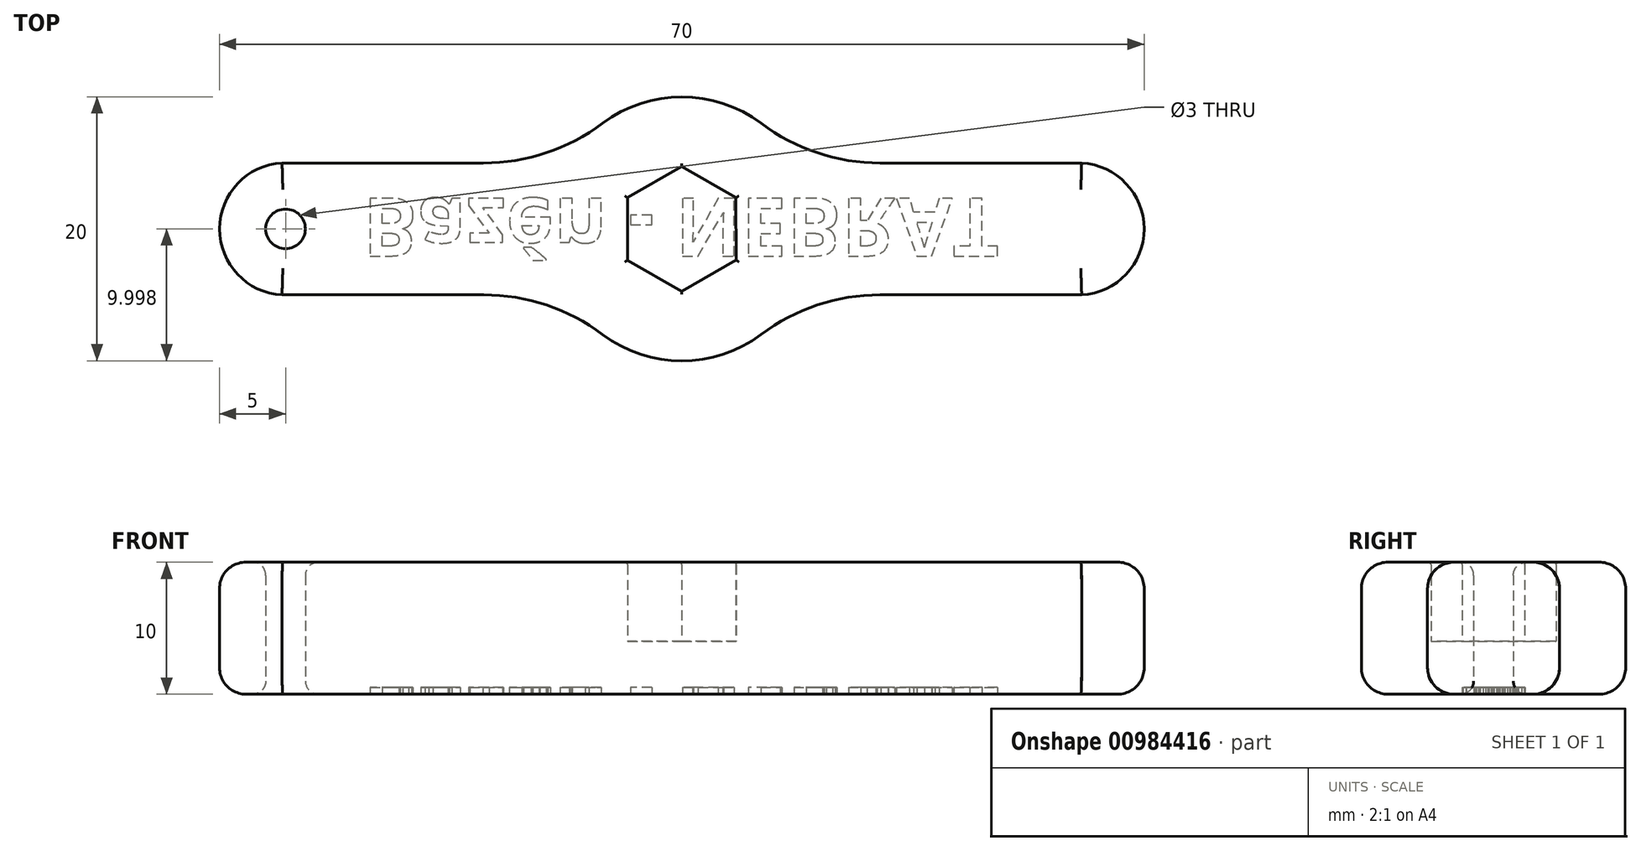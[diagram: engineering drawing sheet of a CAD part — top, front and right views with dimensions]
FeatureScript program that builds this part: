
annotation { "Feature Type Name" : "Feature", "Feature Type Description" : "" }
export const myFeature = defineFeature(function(context is Context, id is Id, definition is map)
    precondition{}
    {
        {
            var Q0;
            Q0=qCreatedBy(makeId("Top.planeOp"),FACE);
            var sketch = newSketch(context, id + "F0", { "sketchPlane" : qUnion([Q0])});
            skCircle(sketch, "E0.cCircle", {"center": v(0, 0) * mm, "radius": 4.1 * mm, "construction": true});
            skLineSegment(sketch, "E0.0", {"start": v(4.1, -2.36) * mm, "end": v(0, -4.73) * mm});
            skLineSegment(sketch, "E0.1", {"start": v(0, -4.73) * mm, "end": v(-4.1, -2.37) * mm});
            skLineSegment(sketch, "E0.2", {"start": v(-4.1, -2.37) * mm, "end": v(-4.1, 2.36) * mm});
            skLineSegment(sketch, "E0.3", {"start": v(-4.1, 2.36) * mm, "end": v(0, 4.73) * mm});
            skLineSegment(sketch, "E0.4", {"start": v(0, 4.73) * mm, "end": v(4.1, 2.37) * mm});
            skLineSegment(sketch, "E0.5", {"start": v(4.1, 2.37) * mm, "end": v(4.1, -2.36) * mm});
            skPoint(sketch, "E0.0.midPoint", {"position": v(2.05, -3.55) * mm});
            skArc(sketch, "E1", {"start": v(6, 8) * mm, "mid": v(0, 10) * mm, "end": v(-6, 8) * mm});
            skArc(sketch, "E2", {"start": v(29.73, -5) * mm, "mid": v(35, 0) * mm, "end": v(29.73, 5) * mm});
            skPoint(sketch, "E2.centerSnap0", {"position": v(-4.1, 0) * mm});
            skLineSegment(sketch, "E3", {"start": v(30.27, 5) * mm, "end": v(15.01, 5) * mm});
            skLineSegment(sketch, "E4", {"start": v(30.27, -5) * mm, "end": v(15, -5) * mm});
            skPoint(sketch, "E5.visualSharp", {"position": v(8.67, 5) * mm});
            skArc(sketch, "E5.filletArc", {"start": v(6, 8) * mm, "mid": v(10.26, 5.76) * mm, "end": v(15.01, 5) * mm});
            skPoint(sketch, "E6.visualSharp", {"position": v(8.66, -5) * mm});
            skArc(sketch, "E6.filletArc", {"start": v(15, -5) * mm, "mid": v(10.26, -5.77) * mm, "end": v(6, -8) * mm});
            skArc(sketch, "E7.MirrorCS", {"start": v(-6, 8) * mm, "mid": v(-10.26, 5.76) * mm, "end": v(-15.01, 5) * mm});
            skLineSegment(sketch, "E8.MirrorCS", {"start": v(-30.27, 5) * mm, "end": v(-15.01, 5) * mm});
            skArc(sketch, "E9.MirrorCS", {"start": v(-29.73, -5) * mm, "mid": v(-35, 0) * mm, "end": v(-29.73, 5) * mm});
            skLineSegment(sketch, "E10.MirrorCS", {"start": v(-30.27, -5) * mm, "end": v(-15, -5) * mm});
            skArc(sketch, "E11.MirrorCS", {"start": v(-15, -5) * mm, "mid": v(-10.26, -5.77) * mm, "end": v(-6, -8) * mm});
            skArc(sketch, "E12.trimOffspring", {"start": v(-6, -8) * mm, "mid": v(0, -10) * mm, "end": v(6, -8) * mm});
            skCircle(sketch, "E13", {"center": v(-30, 0) * mm, "radius": 1.5 * mm});
            skSolve(sketch);
        }
        {
            var Q0;
            Q0=makeQuery(id+"F0.imprint","IMPRINT",FACE,{"disambiguationData":[TD([[makeQuery(id+"F0.imprint","IMPRINT",EDGE,{"derivedFrom":sQuery(id+"F0.wireOp",EDGE,"E0.0")}),1.0]])]});
            extrude(context, id + "F1", {"entities" : qUnion([Q0]), "depth" : 10 * mm, "offsetDistance" : 25 * mm, "symmetric" : true});
        }
        {
            var Q0;
            Q0=makeQuery(id+"F1.opExtrude","CAP_FACE",FACE,{"disambiguationData":[OSD([sQuery(id+"F0.wireOp",EDGE,"E0.0"),sQuery(id+"F0.wireOp",EDGE,"E0.1"),sQuery(id+"F0.wireOp",EDGE,"E0.2"),sQuery(id+"F0.wireOp",EDGE,"E0.3"),sQuery(id+"F0.wireOp",EDGE,"E0.4"),sQuery(id+"F0.wireOp",EDGE,"E0.5"),sQuery(id+"F0.wireOp",EDGE,"E1"),sQuery(id+"F0.wireOp",EDGE,"E2"),sQuery(id+"F0.wireOp",EDGE,"E3"),sQuery(id+"F0.wireOp",EDGE,"E4"),sQuery(id+"F0.wireOp",EDGE,"E5.filletArc"),sQuery(id+"F0.wireOp",EDGE,"E6.filletArc"),sQuery(id+"F0.wireOp",EDGE,"E7.MirrorCS"),sQuery(id+"F0.wireOp",EDGE,"E8.MirrorCS"),sQuery(id+"F0.wireOp",EDGE,"E9.MirrorCS"),sQuery(id+"F0.wireOp",EDGE,"E10.MirrorCS"),sQuery(id+"F0.wireOp",EDGE,"E11.MirrorCS"),sQuery(id+"F0.wireOp",EDGE,"E12.trimOffspring")])],"isStart":true});
            var sketch = newSketch(context, id + "F2", { "sketchPlane" : qUnion([Q0])});
            skCircle(sketch, "E14", {"center": v(0, 0) * mm, "radius": 7.22 * mm});
            skSolve(sketch);
        }
        {
            var Q0;
            Q0 = qSketchRegion(id + "F2", true);
            extrude(context, id + "F3", {"entities" : qUnion([Q0]), "operationType" : NewBodyOperationType.ADD, "oppositeDirection" : true, "depth" : 4 * mm, "offsetDistance" : 25 * mm});
        }
        {
            var Q0;
            Q0=makeQuery(id+"F1.opExtrude","CAP_EDGE",EDGE,{"disambiguationData":[OSD([sQuery(id+"F0.wireOp",EDGE,"E0.3")])],"isStart":false});
            var Q1;
            Q1=makeQuery(id+"F1.opExtrude","CAP_EDGE",EDGE,{"disambiguationData":[OSD([sQuery(id+"F0.wireOp",EDGE,"E0.4")])],"isStart":false});
            var Q2;
            Q2=makeQuery(id+"F1.opExtrude","CAP_EDGE",EDGE,{"disambiguationData":[OSD([sQuery(id+"F0.wireOp",EDGE,"E0.5")])],"isStart":false});
            var Q3;
            Q3=makeQuery(id+"F1.opExtrude","CAP_EDGE",EDGE,{"disambiguationData":[OSD([sQuery(id+"F0.wireOp",EDGE,"E0.0")])],"isStart":false});
            var Q4;
            Q4=makeQuery(id+"F1.opExtrude","CAP_EDGE",EDGE,{"disambiguationData":[OSD([sQuery(id+"F0.wireOp",EDGE,"E0.1")])],"isStart":false});
            var Q5;
            Q5=makeQuery(id+"F1.opExtrude","CAP_EDGE",EDGE,{"disambiguationData":[OSD([sQuery(id+"F0.wireOp",EDGE,"E0.2")])],"isStart":false});
            fillet(context, id + "F4", {"entities" : qUnion([Q0, Q1, Q2, Q3, Q4, Q5]), "radius" : 0.2 * mm, "tangentPropagation" : true, "allowEdgeOverflow" : false});
        }
        {
            var Q0;
            Q0=makeQuery(id+"F3.boolean.opBoolean","MERGE",FACE,{"derivedFrom":[makeQuery(id+"F1.opExtrude","CAP_FACE",FACE,{"disambiguationData":[OSD([sQuery(id+"F0.wireOp",EDGE,"E0.0"),sQuery(id+"F0.wireOp",EDGE,"E0.1"),sQuery(id+"F0.wireOp",EDGE,"E0.2"),sQuery(id+"F0.wireOp",EDGE,"E0.3"),sQuery(id+"F0.wireOp",EDGE,"E0.4"),sQuery(id+"F0.wireOp",EDGE,"E0.5"),sQuery(id+"F0.wireOp",EDGE,"E1"),sQuery(id+"F0.wireOp",EDGE,"E2"),sQuery(id+"F0.wireOp",EDGE,"E3"),sQuery(id+"F0.wireOp",EDGE,"E4"),sQuery(id+"F0.wireOp",EDGE,"E5.filletArc"),sQuery(id+"F0.wireOp",EDGE,"E6.filletArc"),sQuery(id+"F0.wireOp",EDGE,"E7.MirrorCS"),sQuery(id+"F0.wireOp",EDGE,"E8.MirrorCS"),sQuery(id+"F0.wireOp",EDGE,"E9.MirrorCS"),sQuery(id+"F0.wireOp",EDGE,"E10.MirrorCS"),sQuery(id+"F0.wireOp",EDGE,"E11.MirrorCS"),sQuery(id+"F0.wireOp",EDGE,"E12.trimOffspring")])],"isStart":true}),makeQuery(id+"F3.opExtrude","CAP_FACE",FACE,{"disambiguationData":[OSD([sQuery(id+"F2.wireOp",EDGE,"E14")])],"isStart":true})]});
            var sketch = newSketch(context, id + "F5", { "sketchPlane" : qUnion([Q0])});
            skText(sketch, "E15", { "text": "Bazén - NEBRAT", "fontName": "OpenSans-Bold.ttf"});
            const initialGuessF5  = {"E15": [-0.02415, -0.00232, 1, 0, 0.00442]};
            skSetInitialGuess(sketch, initialGuessF5);
            skSolve(sketch);
        }
        {
            var Q0;
            Q0 = qSketchRegion(id + "F5", true);
            extrude(context, id + "F6", {"entities" : qUnion([Q0]), "operationType" : NewBodyOperationType.REMOVE, "oppositeDirection" : true, "depth" : 0.5 * mm, "offsetDistance" : 25 * mm});
        }
        {
            var Q0;
            Q0=makeQuery(id+"F1.opExtrude","CAP_EDGE",EDGE,{"disambiguationData":[OSD([sQuery(id+"F0.wireOp",EDGE,"E13")])],"isStart":false});
            fillet(context, id + "F7", {"entities" : qUnion([Q0]), "radius" : 1 * mm, "tangentPropagation" : true, "allowEdgeOverflow" : false});
        }
        {
            var Q0;
            Q0=makeQuery(id+"F1.opExtrude","CAP_EDGE",EDGE,{"disambiguationData":[OSD([sQuery(id+"F0.wireOp",EDGE,"E2")])],"isStart":true});
            var Q1;
            Q1=makeQuery(id+"F1.opExtrude","CAP_EDGE",EDGE,{"disambiguationData":[OSD([sQuery(id+"F0.wireOp",EDGE,"E3")])],"isStart":true});
            var Q2;
            Q2=makeQuery(id+"F1.opExtrude","CAP_EDGE",EDGE,{"disambiguationData":[OSD([sQuery(id+"F0.wireOp",EDGE,"E5.filletArc")])],"isStart":true});
            var Q3;
            Q3=makeQuery(id+"F1.opExtrude","CAP_EDGE",EDGE,{"disambiguationData":[OSD([sQuery(id+"F0.wireOp",EDGE,"E1")])],"isStart":true});
            var Q4;
            Q4=makeQuery(id+"F1.opExtrude","CAP_EDGE",EDGE,{"disambiguationData":[OSD([sQuery(id+"F0.wireOp",EDGE,"E7.MirrorCS")])],"isStart":true});
            var Q5;
            Q5=makeQuery(id+"F1.opExtrude","CAP_EDGE",EDGE,{"disambiguationData":[OSD([sQuery(id+"F0.wireOp",EDGE,"E8.MirrorCS")])],"isStart":true});
            var Q6;
            Q6=makeQuery(id+"F1.opExtrude","CAP_EDGE",EDGE,{"disambiguationData":[OSD([sQuery(id+"F0.wireOp",EDGE,"E9.MirrorCS")])],"isStart":true});
            var Q7;
            Q7=makeQuery(id+"F1.opExtrude","CAP_EDGE",EDGE,{"disambiguationData":[OSD([sQuery(id+"F0.wireOp",EDGE,"E10.MirrorCS")])],"isStart":true});
            var Q8;
            Q8=makeQuery(id+"F1.opExtrude","CAP_EDGE",EDGE,{"disambiguationData":[OSD([sQuery(id+"F0.wireOp",EDGE,"E11.MirrorCS")])],"isStart":true});
            var Q9;
            Q9=makeQuery(id+"F1.opExtrude","CAP_EDGE",EDGE,{"disambiguationData":[OSD([sQuery(id+"F0.wireOp",EDGE,"E12.trimOffspring")])],"isStart":true});
            var Q10;
            Q10=makeQuery(id+"F1.opExtrude","CAP_EDGE",EDGE,{"disambiguationData":[OSD([sQuery(id+"F0.wireOp",EDGE,"E6.filletArc")])],"isStart":true});
            var Q11;
            Q11=makeQuery(id+"F1.opExtrude","CAP_EDGE",EDGE,{"disambiguationData":[OSD([sQuery(id+"F0.wireOp",EDGE,"E4")])],"isStart":true});
            var Q12;
            Q12=makeQuery(id+"F1.opExtrude","CAP_EDGE",EDGE,{"disambiguationData":[OSD([sQuery(id+"F0.wireOp",EDGE,"E8.MirrorCS")])],"isStart":false});
            var Q13;
            Q13=makeQuery(id+"F1.opExtrude","CAP_EDGE",EDGE,{"disambiguationData":[OSD([sQuery(id+"F0.wireOp",EDGE,"E7.MirrorCS")])],"isStart":false});
            var Q14;
            Q14=makeQuery(id+"F1.opExtrude","CAP_EDGE",EDGE,{"disambiguationData":[OSD([sQuery(id+"F0.wireOp",EDGE,"E1")])],"isStart":false});
            var Q15;
            Q15=makeQuery(id+"F1.opExtrude","CAP_EDGE",EDGE,{"disambiguationData":[OSD([sQuery(id+"F0.wireOp",EDGE,"E5.filletArc")])],"isStart":false});
            var Q16;
            Q16=makeQuery(id+"F1.opExtrude","CAP_EDGE",EDGE,{"disambiguationData":[OSD([sQuery(id+"F0.wireOp",EDGE,"E3")])],"isStart":false});
            var Q17;
            Q17=makeQuery(id+"F1.opExtrude","CAP_EDGE",EDGE,{"disambiguationData":[OSD([sQuery(id+"F0.wireOp",EDGE,"E2")])],"isStart":false});
            var Q18;
            Q18=makeQuery(id+"F1.opExtrude","CAP_EDGE",EDGE,{"disambiguationData":[OSD([sQuery(id+"F0.wireOp",EDGE,"E4")])],"isStart":false});
            var Q19;
            Q19=makeQuery(id+"F1.opExtrude","CAP_EDGE",EDGE,{"disambiguationData":[OSD([sQuery(id+"F0.wireOp",EDGE,"E6.filletArc")])],"isStart":false});
            var Q20;
            Q20=makeQuery(id+"F1.opExtrude","CAP_EDGE",EDGE,{"disambiguationData":[OSD([sQuery(id+"F0.wireOp",EDGE,"E12.trimOffspring")])],"isStart":false});
            var Q21;
            Q21=makeQuery(id+"F1.opExtrude","CAP_EDGE",EDGE,{"disambiguationData":[OSD([sQuery(id+"F0.wireOp",EDGE,"E11.MirrorCS")])],"isStart":false});
            var Q22;
            Q22=makeQuery(id+"F1.opExtrude","CAP_EDGE",EDGE,{"disambiguationData":[OSD([sQuery(id+"F0.wireOp",EDGE,"E10.MirrorCS")])],"isStart":false});
            var Q23;
            Q23=makeQuery(id+"F1.opExtrude","CAP_EDGE",EDGE,{"disambiguationData":[OSD([sQuery(id+"F0.wireOp",EDGE,"E9.MirrorCS")])],"isStart":false});
            fillet(context, id + "F8", {"entities" : qUnion([Q0, Q1, Q2, Q3, Q4, Q5, Q6, Q7, Q8, Q9, Q10, Q11, Q12, Q13, Q14, Q15, Q16, Q17, Q18, Q19, Q20, Q21, Q22, Q23]), "radius" : 2 * mm, "tangentPropagation" : true, "allowEdgeOverflow" : false});
        }
        {
            var Q0;
            Q0=makeQuery(id+"F1.opExtrude","CAP_EDGE",EDGE,{"disambiguationData":[OSD([sQuery(id+"F0.wireOp",EDGE,"E13")])],"isStart":true});
            fillet(context, id + "F9", {"entities" : qUnion([Q0]), "radius" : 1 * mm, "tangentPropagation" : true, "allowEdgeOverflow" : false});
        }
    });
